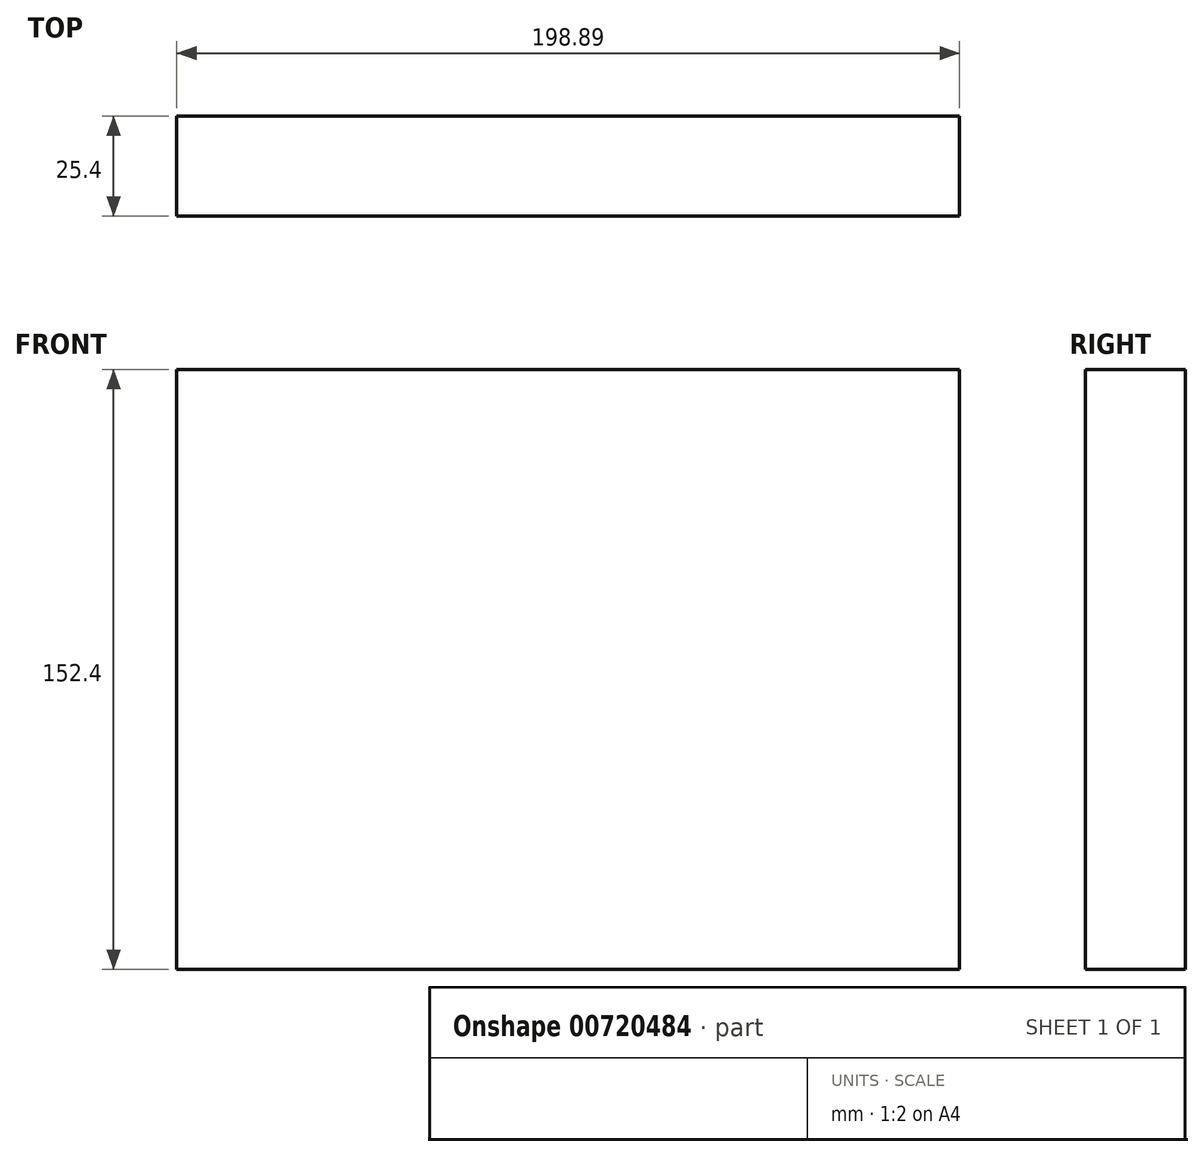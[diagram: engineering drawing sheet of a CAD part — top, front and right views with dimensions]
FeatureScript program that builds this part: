
annotation { "Feature Type Name" : "Feature", "Feature Type Description" : "" }
export const myFeature = defineFeature(function(context is Context, id is Id, definition is map)
    precondition{}
    {
        {
            var Q0;
            Q0=qCreatedBy(makeId("Front.planeOp"),FACE);
            var sketch = newSketch(context, id + "F0", { "sketchPlane" : qUnion([Q0])});
            skLineSegment(sketch, "E0.bottom", {"start": v(-99.75, 24.02) * mm, "end": v(99.14, 24.02) * mm});
            skLineSegment(sketch, "E0.top", {"start": v(-99.75, -128.38) * mm, "end": v(99.14, -128.38) * mm});
            skLineSegment(sketch, "E0.left", {"start": v(-99.75, 24.02) * mm, "end": v(-99.75, -128.38) * mm});
            skLineSegment(sketch, "E0.right", {"start": v(99.14, 24.02) * mm, "end": v(99.14, -128.38) * mm});
            skSolve(sketch);
        }
        {
            var Q0;
            Q0=makeQuery(id+"F0.imprint","IMPRINT",FACE,{"disambiguationData":[TD([[makeQuery(id+"F0.imprint","IMPRINT",EDGE,{"derivedFrom":sQuery(id+"F0.wireOp",EDGE,"E0.bottom")}),-1.0]])]});
            extrude(context, id + "F1", {"entities" : qUnion([Q0]), "depth" : 25.4 * mm, "offsetDistance" : 25.4 * mm});
        }
    });
